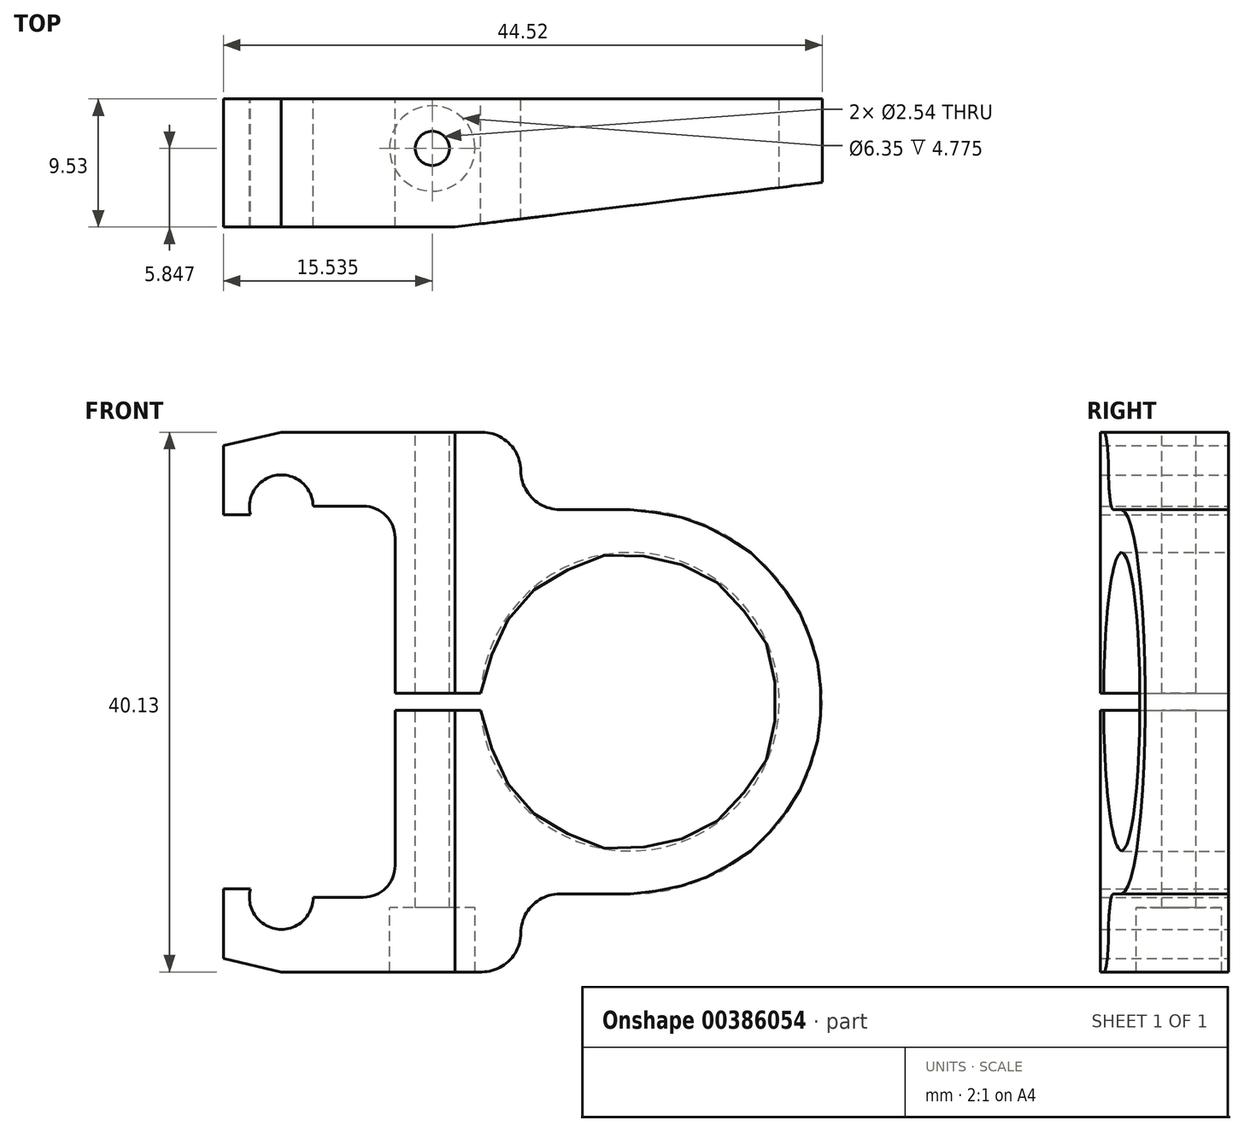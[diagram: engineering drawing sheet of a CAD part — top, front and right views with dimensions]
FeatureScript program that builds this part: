
annotation { "Feature Type Name" : "Feature", "Feature Type Description" : "" }
export const myFeature = defineFeature(function(context is Context, id is Id, definition is map)
    precondition{}
    {
        {
            var Q0;
            Q0=qCreatedBy(makeId("Front.planeOp"),FACE);
            var sketch = newSketch(context, id + "F0", { "sketchPlane" : qUnion([Q0])});
            skArc(sketch, "E0", {"start": v(-23.56, 14.54) * mm, "mid": v(-26.24, 16.84) * mm, "end": v(-28.2, 13.9) * mm});
            skArc(sketch, "E1", {"start": v(-28.2, -13.9) * mm, "mid": v(-26.24, -16.9) * mm, "end": v(-23.55, -14.54) * mm});
            skLineSegment(sketch, "E2", {"start": v(-23.55, -14.54) * mm, "end": v(-19.82, -14.54) * mm});
            skLineSegment(sketch, "E3", {"start": v(-23.56, 14.54) * mm, "end": v(-19.82, 14.54) * mm});
            skArc(sketch, "E4", {"start": v(-11, 20.04) * mm, "mid": v(-8.96, 19.2) * mm, "end": v(-8.12, 17.16) * mm});
            skArc(sketch, "E5", {"start": v(-8.12, 17.16) * mm, "mid": v(-7.26, 15.13) * mm, "end": v(-5.22, 14.29) * mm});
            skLineSegment(sketch, "E6", {"start": v(0, 14.29) * mm, "end": v(-5.22, 14.29) * mm});
            skLineSegment(sketch, "E7", {"start": v(-11, 20.04) * mm, "end": v(-25.92, 20.04) * mm});
            skArc(sketch, "E8", {"start": v(0, 14.29) * mm, "mid": v(14.29, 0) * mm, "end": v(0, -14.29) * mm});
            skLineSegment(sketch, "E9", {"start": v(0, -14.29) * mm, "end": v(-5.22, -14.29) * mm});
            skArc(sketch, "E10", {"start": v(-5.22, -14.29) * mm, "mid": v(-7.27, -15.14) * mm, "end": v(-8.12, -17.19) * mm});
            skArc(sketch, "E11", {"start": v(-8.12, -17.19) * mm, "mid": v(-8.96, -19.24) * mm, "end": v(-11.01, -20.1) * mm});
            skLineSegment(sketch, "E12", {"start": v(-11.01, -20.1) * mm, "end": v(-25.92, -20.1) * mm});
            skLineSegment(sketch, "E13", {"start": v(-28.2, -13.9) * mm, "end": v(-30.23, -13.9) * mm});
            skLineSegment(sketch, "E14", {"start": v(-28.2, 13.9) * mm, "end": v(-30.23, 13.9) * mm});
            skLineSegment(sketch, "E15", {"start": v(-30.23, 13.9) * mm, "end": v(-30.23, 19.03) * mm});
            skLineSegment(sketch, "E16", {"start": v(-30.23, -13.9) * mm, "end": v(-30.23, -19.07) * mm});
            skLineSegment(sketch, "E17", {"start": v(-30.23, -19.07) * mm, "end": v(-25.92, -20.1) * mm});
            skLineSegment(sketch, "E18", {"start": v(-30.23, 19.03) * mm, "end": v(-25.92, 20.04) * mm});
            skLineSegment(sketch, "E19", {"start": v(-17.46, 0.64) * mm, "end": v(-11.09, 0.64) * mm});
            skLineSegment(sketch, "E20", {"start": v(-17.46, -0.63) * mm, "end": v(-11.09, -0.63) * mm});
            skArc(sketch, "E21", {"start": v(-11.09, -0.63) * mm, "mid": v(11.1, 0) * mm, "end": v(-11.09, 0.64) * mm});
            skLineSegment(sketch, "E22", {"start": v(-17.46, 12.18) * mm, "end": v(-17.46, 0.64) * mm});
            skLineSegment(sketch, "E23", {"start": v(-17.46, -0.63) * mm, "end": v(-17.46, -12.18) * mm});
            skPoint(sketch, "E24.visualSharp", {"position": v(-17.46, 14.54) * mm});
            skArc(sketch, "E24.filletArc", {"start": v(-17.46, 12.18) * mm, "mid": v(-18.15, 13.85) * mm, "end": v(-19.82, 14.54) * mm});
            skPoint(sketch, "E25.visualSharp", {"position": v(-17.46, -14.54) * mm});
            skArc(sketch, "E25.filletArc", {"start": v(-19.82, -14.54) * mm, "mid": v(-18.15, -13.85) * mm, "end": v(-17.46, -12.18) * mm});
            skCircle(sketch, "E26", {"center": v(-45.34, 20.05) * mm, "radius": 1.27 * mm});
            skLineSegment(sketch, "E27", {"start": v(14.29, 0) * mm, "end": v(14.29, 17.57) * mm});
            skSolve(sketch);
        }
        {
            var Q0;
            Q0=makeQuery(id+"F0.imprint","IMPRINT",FACE,{"disambiguationData":[TD([[makeQuery(id+"F0.imprint","IMPRINT",EDGE,{"derivedFrom":sQuery(id+"F0.wireOp",EDGE,"E0")}),-1.0]])]});
            extrude(context, id + "F1", {"entities" : qUnion([Q0]), "depth" : 9.52 * mm, "offsetDistance" : 25.4 * mm});
        }
        {
            var Q0;
            Q0=makeQuery(id+"F1.opExtrude","SWEPT_FACE",FACE,{"disambiguationData":[OSD([sQuery(id+"F0.wireOp",EDGE,"E12")])]});
            var sketch = newSketch(context, id + "F2", { "sketchPlane" : qUnion([Q0])});
            skPoint(sketch, "E28", {"position": v(-14.7, 3.68) * mm});
            skSolve(sketch);
        }
        {
            var Q0;
            Q0=sQuery(id+"F2.wireOp",VERTEX,"E28");
            var Q1;
            Q1=makeQuery(id+"F1.opExtrude","SWEPT_BODY",BODY,{"disambiguationData":[OSD([sQuery(id+"F0.wireOp",EDGE,"E0"),sQuery(id+"F0.wireOp",EDGE,"E1"),sQuery(id+"F0.wireOp",EDGE,"E2"),sQuery(id+"F0.wireOp",EDGE,"E3"),sQuery(id+"F0.wireOp",EDGE,"E4"),sQuery(id+"F0.wireOp",EDGE,"E5"),sQuery(id+"F0.wireOp",EDGE,"E6"),sQuery(id+"F0.wireOp",EDGE,"E7"),sQuery(id+"F0.wireOp",EDGE,"E8"),sQuery(id+"F0.wireOp",EDGE,"E9"),sQuery(id+"F0.wireOp",EDGE,"E10"),sQuery(id+"F0.wireOp",EDGE,"E11"),sQuery(id+"F0.wireOp",EDGE,"E12"),sQuery(id+"F0.wireOp",EDGE,"E13"),sQuery(id+"F0.wireOp",EDGE,"E14"),sQuery(id+"F0.wireOp",EDGE,"E15"),sQuery(id+"F0.wireOp",EDGE,"E16"),sQuery(id+"F0.wireOp",EDGE,"E17"),sQuery(id+"F0.wireOp",EDGE,"E18"),sQuery(id+"F0.wireOp",EDGE,"E19"),sQuery(id+"F0.wireOp",EDGE,"E20"),sQuery(id+"F0.wireOp",EDGE,"E21"),sQuery(id+"F0.wireOp",EDGE,"E22"),sQuery(id+"F0.wireOp",EDGE,"E23")])]});
            hole(context, id + "F3", {"style" : HoleStyle.C_BORE, "endStyle" : HoleEndStyle.THROUGH, "holeDiameter" : 2.54 * mm, "cBoreDiameter" : 6.35 * mm, "cBoreDepth" : 4.78 * mm, "majorDiameter" : 6.35 * mm, "isTappedThrough" : true, "tappedDepth" : 12.7 * mm, "tapClearance" : 3, "locations" : qUnion([Q0]), "scope" : qUnion([Q1])});
        }
        {
            var Q0;
            Q0=qCreatedBy(makeId("Top.planeOp"),FACE);
            var sketch = newSketch(context, id + "F4", { "sketchPlane" : qUnion([Q0])});
            skLineSegment(sketch, "E29", {"start": v(-13.63, -9.6) * mm, "end": v(14.5, -6.17) * mm});
            skLineSegment(sketch, "E30", {"start": v(14.5, -6.17) * mm, "end": v(14.5, -10.02) * mm});
            skLineSegment(sketch, "E31", {"start": v(14.5, -10.02) * mm, "end": v(-13.63, -9.6) * mm});
            skSolve(sketch);
        }
        {
            var Q0;
            Q0=makeQuery(id+"F4.imprint","IMPRINT",FACE,{"disambiguationData":[TD([[makeQuery(id+"F4.imprint","IMPRINT",EDGE,{"derivedFrom":sQuery(id+"F4.wireOp",EDGE,"E29")}),-1.0]])]});
            extrude(context, id + "F5", {"entities" : qUnion([Q0]), "operationType" : NewBodyOperationType.REMOVE, "depth" : 40.64 * mm, "offsetDistance" : 25.4 * mm, "symmetric" : true});
        }
    });
